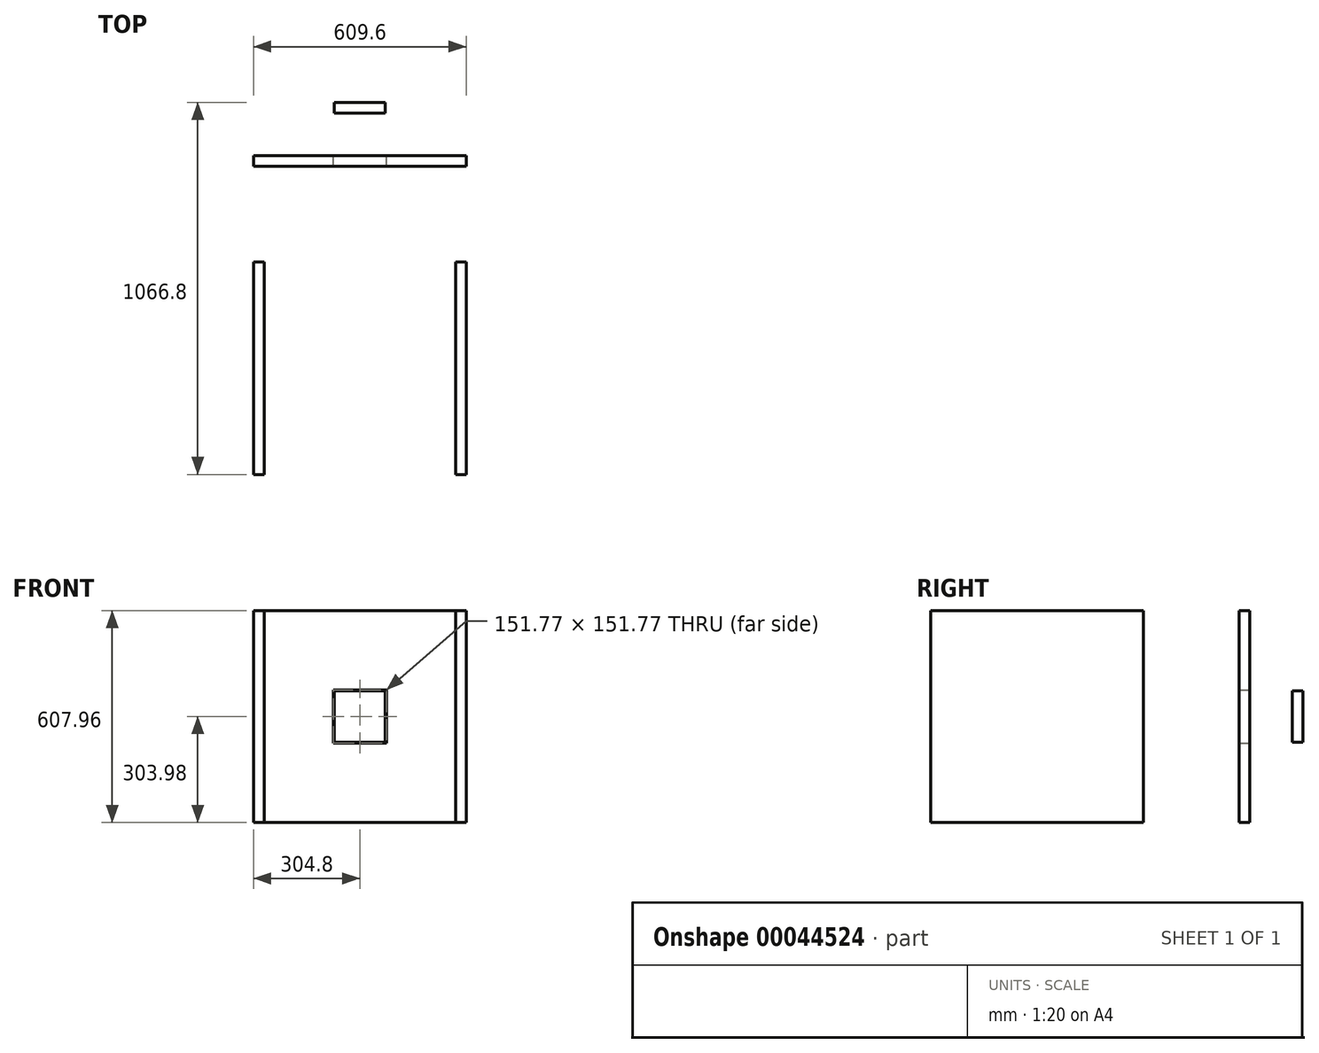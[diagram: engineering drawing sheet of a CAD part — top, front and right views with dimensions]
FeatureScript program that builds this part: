
annotation { "Feature Type Name" : "Feature", "Feature Type Description" : "" }
export const myFeature = defineFeature(function(context is Context, id is Id, definition is map)
    precondition{}
    {
        {
            var Q0;
            Q0=qCreatedBy(makeId("Front.planeOp"),FACE);
            var sketch = newSketch(context, id + "F0", { "sketchPlane" : qUnion([Q0])});
            skLineSegment(sketch, "E0", {"start": v(0, 0) * mm, "end": v(0, 303.98) * mm});
            skLineSegment(sketch, "E1", {"start": v(0, 303.98) * mm, "end": v(0, 0) * mm});
            skLineSegment(sketch, "E2", {"start": v(0, 0) * mm, "end": v(303.99, 0) * mm});
            skLineSegment(sketch, "E3.MirrorCS", {"start": v(0, -303.98) * mm, "end": v(0, 0) * mm});
            skLineSegment(sketch, "E4.MirrorCS", {"start": v(0, 0) * mm, "end": v(-303.99, 0) * mm});
            skLineSegment(sketch, "E5", {"start": v(0, 303.98) * mm, "end": v(304.8, 303.98) * mm});
            skLineSegment(sketch, "E6.MirrorCS", {"start": v(0, 303.98) * mm, "end": v(-304.8, 303.98) * mm});
            skLineSegment(sketch, "E7.MirrorCS", {"start": v(0, -303.98) * mm, "end": v(304.8, -303.98) * mm});
            skLineSegment(sketch, "E8.MirrorCS", {"start": v(0, -303.98) * mm, "end": v(-304.8, -303.98) * mm});
            skLineSegment(sketch, "E9", {"start": v(304.8, 303.98) * mm, "end": v(304.8, -303.98) * mm});
            skLineSegment(sketch, "E10", {"start": v(-304.8, 303.98) * mm, "end": v(-304.8, -303.98) * mm});
            skSolve(sketch);
        }
        {
            var Q0;
            Q0=sQuery(id+"F0.wireOp",EDGE,"E7.MirrorCS");
            var Q1;
            Q1=sQuery(id+"F0.wireOp",EDGE,"E9");
            var Q2;
            Q2=sQuery(id+"F0.wireOp",EDGE,"E8.MirrorCS");
            var Q3;
            Q3=sQuery(id+"F0.wireOp",EDGE,"E10");
            extrude(context, id + "F1", {"bodyType" : ToolBodyType.SURFACE, "surfaceEntities" : qUnion([Q0, Q1, Q2, Q3]), "oppositeDirection" : true, "depth" : 609.6 * mm});
        }
        {
            var Q0;
            Q0=qCreatedBy(makeId("Front.planeOp"),FACE);
            cPlane(context, id + "F2", {"entities" : qUnion([Q0]), "cplaneType" : CPlaneType.OFFSET, "offset" : 914.4 * mm, "oppositeDirection" : true, "width" : 152.4 * mm, "height" : 152.4 * mm});
        }
        {
            var Q0;
            Q0=qCreatedBy(id+"F2.planeOp",FACE);
            var sketch = newSketch(context, id + "F3", { "sketchPlane" : qUnion([Q0])});
            skLineSegment(sketch, "E11.rect.bottom", {"start": v(-304.55, -303.54) * mm, "end": v(304.55, -303.54) * mm});
            skLineSegment(sketch, "E11.rect.top", {"start": v(-304.55, 303.54) * mm, "end": v(304.55, 303.54) * mm});
            skLineSegment(sketch, "E11.rect.left", {"start": v(-304.55, -303.54) * mm, "end": v(-304.55, 303.54) * mm});
            skLineSegment(sketch, "E11.rect.right", {"start": v(304.55, -303.54) * mm, "end": v(304.55, 303.54) * mm});
            skPoint(sketch, "E11.rect.middle", {"position": v(0, 0) * mm});
            skLineSegment(sketch, "E12.rect.bottom", {"start": v(-75.88, -75.89) * mm, "end": v(75.88, -75.89) * mm});
            skLineSegment(sketch, "E12.rect.top", {"start": v(-75.88, 75.89) * mm, "end": v(75.88, 75.89) * mm});
            skLineSegment(sketch, "E12.rect.left", {"start": v(-75.88, -75.89) * mm, "end": v(-75.88, 75.89) * mm});
            skLineSegment(sketch, "E12.rect.right", {"start": v(75.88, -75.89) * mm, "end": v(75.88, 75.89) * mm});
            skSolve(sketch);
        }
        {
            var Q0;
            Q0=makeQuery(id+"F3.imprint","IMPRINT",FACE,{"disambiguationData":[TD([[makeQuery(id+"F3.imprint","IMPRINT",EDGE,{"derivedFrom":sQuery(id+"F3.wireOp",EDGE,"E11.rect.bottom")}),1.0]])]});
            extrude(context, id + "F4", {"entities" : qUnion([Q0]), "depth" : 30.48 * mm});
        }
        {
            var Q0;
            Q0=qCreatedBy(makeId("Front.planeOp"),FACE);
            var sketch = newSketch(context, id + "F5", { "sketchPlane" : qUnion([Q0])});
            skLineSegment(sketch, "E13.rect.bottom", {"start": v(304.55, -194.27) * mm, "end": v(-304.55, -194.27) * mm});
            skLineSegment(sketch, "E13.rect.top", {"start": v(304.55, -254.97) * mm, "end": v(-304.55, -254.97) * mm});
            skLineSegment(sketch, "E13.rect.left", {"start": v(304.55, -194.27) * mm, "end": v(304.55, -254.97) * mm});
            skLineSegment(sketch, "E13.rect.right", {"start": v(-304.55, -194.27) * mm, "end": v(-304.55, -254.97) * mm});
            skPoint(sketch, "E13.rect.middle", {"position": v(0, -224.62) * mm});
            skSolve(sketch);
        }
        {
            var Q0;
            Q0=sQuery(id+"F5.wireOp",EDGE,"E13.rect.top");
            extrude(context, id + "F6", {"bodyType" : ToolBodyType.SURFACE, "surfaceEntities" : qUnion([Q0]), "oppositeDirection" : true, "depth" : 609.6 * mm});
        }
        {
            var Q0;
            Q0=sQuery(id+"F5.wireOp",EDGE,"E13.rect.bottom");
            extrude(context, id + "F7", {"bodyType" : ToolBodyType.SURFACE, "surfaceEntities" : qUnion([Q0]), "oppositeDirection" : true, "depth" : 609.6 * mm});
        }
        {
            var Q0;
            Q0=makeQuery(id+"F1.opExtrude","SWEPT_FACE",FACE,{"disambiguationData":[OSD([sQuery(id+"F0.wireOp",EDGE,"E10")])]});
            extrude(context, id + "F8", {"entities" : qUnion([Q0]), "depth" : 30.48 * mm});
        }
        {
            var Q0;
            Q0=makeQuery(id+"F1.opExtrude","SWEPT_FACE",FACE,{"disambiguationData":[OSD([sQuery(id+"F0.wireOp",EDGE,"E9")])]});
            extrude(context, id + "F9", {"entities" : qUnion([Q0]), "depth" : 30.48 * mm});
        }
        {
            var Q0;
            Q0=makeQuery(id+"F3.imprint","IMPRINT",FACE,{"disambiguationData":[TD([[makeQuery(id+"F3.imprint","IMPRINT",EDGE,{"derivedFrom":sQuery(id+"F3.wireOp",EDGE,"E12.rect.bottom")}),1.0]])]});
            cPlane(context, id + "F10", {"entities" : qUnion([Q0]), "cplaneType" : CPlaneType.OFFSET, "offset" : 152.4 * mm, "oppositeDirection" : true, "width" : 152.4 * mm, "height" : 152.4 * mm});
        }
        {
            var Q0;
            Q0=qCreatedBy(id+"F10.planeOp",FACE);
            var sketch = newSketch(context, id + "F11", { "sketchPlane" : qUnion([Q0])});
            skLineSegment(sketch, "E14.rect.bottom", {"start": v(-72.8, -73.91) * mm, "end": v(72.8, -73.91) * mm});
            skLineSegment(sketch, "E14.rect.top", {"start": v(-72.8, 73.91) * mm, "end": v(72.8, 73.91) * mm});
            skLineSegment(sketch, "E14.rect.left", {"start": v(-72.8, -73.91) * mm, "end": v(-72.8, 73.91) * mm});
            skLineSegment(sketch, "E14.rect.right", {"start": v(72.8, -73.91) * mm, "end": v(72.8, 73.91) * mm});
            skPoint(sketch, "E14.rect.middle", {"position": v(0, 0) * mm});
            skSolve(sketch);
        }
        {
            var Q0;
            Q0=makeQuery(id+"F11.imprint","IMPRINT",FACE,{"disambiguationData":[TD([[makeQuery(id+"F11.imprint","IMPRINT",EDGE,{"derivedFrom":sQuery(id+"F11.wireOp",EDGE,"E14.rect.bottom")}),1.0]])]});
            extrude(context, id + "F12", {"entities" : qUnion([Q0]), "depth" : 30.48 * mm});
        }
    });
